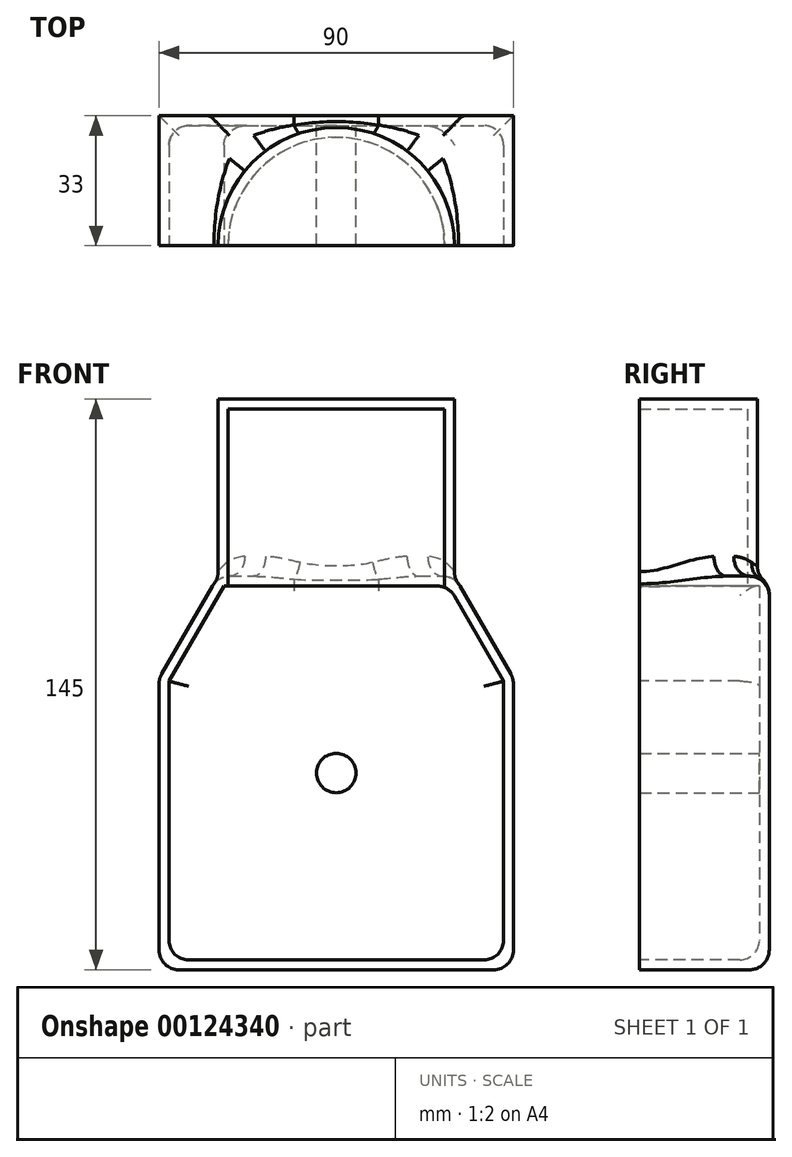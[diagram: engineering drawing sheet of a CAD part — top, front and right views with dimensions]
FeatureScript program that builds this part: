
annotation { "Feature Type Name" : "Feature", "Feature Type Description" : "" }
export const myFeature = defineFeature(function(context is Context, id is Id, definition is map)
    precondition{}
    {
        {
            var Q0;
            Q0=qCreatedBy(makeId("Front.planeOp"),FACE);
            var sketch = newSketch(context, id + "F0", { "sketchPlane" : qUnion([Q0])});
            skLineSegment(sketch, "E0.bottom", {"start": v(-30, 100) * mm, "end": v(30, 100) * mm});
            skLineSegment(sketch, "E0.top", {"start": v(-45, 0) * mm, "end": v(45, 0) * mm});
            skLineSegment(sketch, "E0.left", {"start": v(-45, 74.02) * mm, "end": v(-45, 0) * mm});
            skLineSegment(sketch, "E0.right", {"start": v(45, 74.02) * mm, "end": v(45, 0) * mm});
            skLineSegment(sketch, "E1.top", {"start": v(-30, 145) * mm, "end": v(30, 145) * mm});
            skLineSegment(sketch, "E1.left", {"start": v(-30, 100) * mm, "end": v(-30, 145) * mm});
            skLineSegment(sketch, "E1.right", {"start": v(30, 100) * mm, "end": v(30, 145) * mm});
            skLineSegment(sketch, "E2", {"start": v(0, 0) * mm, "end": v(0, 230.65) * mm, "construction": true});
            skLineSegment(sketch, "E3", {"start": v(-30, 100) * mm, "end": v(-45, 74.02) * mm});
            skLineSegment(sketch, "E4", {"start": v(30, 100) * mm, "end": v(45, 74.02) * mm});
            skLineSegment(sketch, "E5", {"start": v(0, 100) * mm, "end": v(0, 145) * mm});
            skSolve(sketch);
        }
        {
            var Q0;
            {var subQ0=sQuery(id+"F0.wireOp",EDGE,"E1.right");Q0=makeQuery(id+"F0.imprint","IMPRINT",FACE,{"disambiguationData":[TD([[makeQuery(id+"F0.imprint","IMPRINT",EDGE,{"derivedFrom":subQ0}),1.0]])]});}
            var Q1;
            Q1=sQuery(id+"F0.wireOp",EDGE,"E2");
            revolve(context, id + "F1", {"entities" : qUnion([Q0]), "axis" : qUnion([Q1]), "revolveType" : RevolveType.ONE_DIRECTION, "angle" : 180 * degree});
        }
        {
            var Q0;
            Q0=makeQuery(id+"F0.imprint","IMPRINT",FACE,{"disambiguationData":[TD([[makeQuery(id+"F0.imprint","IMPRINT",EDGE,{"derivedFrom":sQuery(id+"F0.wireOp",EDGE,"E0.top")}),1.0]])]});
            extrude(context, id + "F2", {"entities" : qUnion([Q0]), "operationType" : NewBodyOperationType.ADD, "oppositeDirection" : true, "depth" : 33 * mm});
        }
        {
            var Q0;
            {var subQ0=sQuery(id+"F0.wireOp",EDGE,"E0.bottom");Q0=makeQuery(id+"F2.boolean.opBoolean","MERGE",FACE,{"derivedFrom":[makeQuery(id+"F1.opRevolve","CAP_FACE",FACE,{"disambiguationData":[OSD([subQ0,sQuery(id+"F0.wireOp",EDGE,"E1.top"),sQuery(id+"F0.wireOp",EDGE,"E1.right"),sQuery(id+"F0.wireOp",EDGE,"E5")])],"isStart":false}),makeQuery(id+"F2.opExtrude","CAP_FACE",FACE,{"disambiguationData":[OSD([sQuery(id+"F0.wireOp",EDGE,"E0.top"),sQuery(id+"F0.wireOp",EDGE,"E0.left"),sQuery(id+"F0.wireOp",EDGE,"E0.right"),subQ0,sQuery(id+"F0.wireOp",EDGE,"E3"),sQuery(id+"F0.wireOp",EDGE,"E4")])],"isStart":true})]});}
            shell(context, id + "F3", {"entities" : qUnion([Q0]), "thickness" : 2.5 * mm});
        }
        {
            var Q0;
            Q0=makeQuery(id+"F2.opExtrude","SWEPT_EDGE",EDGE,{"disambiguationData":[OSD([sQuery(id+"F0.wireOp",EDGE,"E0.bottom"),sQuery(id+"F0.wireOp",EDGE,"E1.right"),sQuery(id+"F0.wireOp",EDGE,"E4")])]});
            var Q1;
            Q1=makeQuery(id+"F2.opExtrude","SWEPT_EDGE",EDGE,{"disambiguationData":[OSD([sQuery(id+"F0.wireOp",EDGE,"E0.right"),sQuery(id+"F0.wireOp",EDGE,"E4")])]});
            var Q2;
            Q2=makeQuery(id+"F2.opExtrude","SWEPT_EDGE",EDGE,{"disambiguationData":[OSD([sQuery(id+"F0.wireOp",EDGE,"E0.top"),sQuery(id+"F0.wireOp",EDGE,"E0.right")])]});
            var Q3;
            Q3=makeQuery(id+"F2.opExtrude","CAP_EDGE",EDGE,{"disambiguationData":[OSD([sQuery(id+"F0.wireOp",EDGE,"E0.bottom")])],"isStart":false});
            var Q4;
            Q4=makeQuery(id+"F2.opExtrude","CAP_EDGE",EDGE,{"disambiguationData":[OSD([sQuery(id+"F0.wireOp",EDGE,"E0.top")])],"isStart":false});
            var Q5;
            Q5=makeQuery(id+"F2.opExtrude","SWEPT_EDGE",EDGE,{"disambiguationData":[OSD([sQuery(id+"F0.wireOp",EDGE,"E0.bottom"),sQuery(id+"F0.wireOp",EDGE,"E1.left"),sQuery(id+"F0.wireOp",EDGE,"E3")])]});
            var Q6;
            Q6=makeQuery(id+"F2.opExtrude","SWEPT_EDGE",EDGE,{"disambiguationData":[OSD([sQuery(id+"F0.wireOp",EDGE,"E0.left"),sQuery(id+"F0.wireOp",EDGE,"E3")])]});
            var Q7;
            Q7=makeQuery(id+"F2.opExtrude","SWEPT_EDGE",EDGE,{"disambiguationData":[OSD([sQuery(id+"F0.wireOp",EDGE,"E0.top"),sQuery(id+"F0.wireOp",EDGE,"E0.left")])]});
            var Q8;
            {var subQ0=sQuery(id+"F0.wireOp",EDGE,"E0.left");Q8=makeQuery(id+"F3.opShell","OFFSET_EDGE",EDGE,{"disambiguationData":[OSD([subQ0]),TDD([makeQuery(id+"F2.opExtrude","CAP_EDGE",EDGE,{"disambiguationData":[OSD([subQ0])],"isStart":false})])]});}
            var Q9;
            {var subQ0=sQuery(id+"F0.wireOp",EDGE,"E3");Q9=makeQuery(id+"F3.opShell","OFFSET_EDGE",EDGE,{"disambiguationData":[OSD([subQ0]),TDD([makeQuery(id+"F2.opExtrude","CAP_EDGE",EDGE,{"disambiguationData":[OSD([subQ0])],"isStart":false})])]});}
            var Q10;
            {var subQ0=sQuery(id+"F0.wireOp",EDGE,"E4");Q10=makeQuery(id+"F3.opShell","OFFSET_EDGE",EDGE,{"disambiguationData":[OSD([subQ0]),TDD([makeQuery(id+"F2.opExtrude","CAP_EDGE",EDGE,{"disambiguationData":[OSD([subQ0])],"isStart":false})])]});}
            var Q11;
            {var subQ0=sQuery(id+"F0.wireOp",EDGE,"E4");var subQ1=sQuery(id+"F0.wireOp",EDGE,"E1.right");var subQ2=sQuery(id+"F0.wireOp",EDGE,"E0.bottom");Q11=makeQuery(id+"F3.opShell","OFFSET_EDGE",EDGE,{"disambiguationData":[OSD([subQ2,subQ1,subQ0]),TDD([makeQuery(id+"F1.opRevolve","SWEPT_EDGE",EDGE,{"disambiguationData":[OSD([subQ2,subQ1,subQ0])]})])]});}
            var Q12;
            {var subQ0=sQuery(id+"F0.wireOp",EDGE,"E0.right");Q12=makeQuery(id+"F3.opShell","OFFSET_EDGE",EDGE,{"disambiguationData":[OSD([subQ0]),TDD([makeQuery(id+"F2.opExtrude","CAP_EDGE",EDGE,{"disambiguationData":[OSD([subQ0])],"isStart":false})])]});}
            var Q13;
            {var subQ0=sQuery(id+"F0.wireOp",EDGE,"E0.top");Q13=makeQuery(id+"F3.opShell","OFFSET_EDGE",EDGE,{"disambiguationData":[OSD([subQ0]),TDD([makeQuery(id+"F2.opExtrude","CAP_EDGE",EDGE,{"disambiguationData":[OSD([subQ0])],"isStart":false})])]});}
            var Q14;
            Q14=makeQuery(id+"F3.opShell","OFFSET_EDGE",EDGE,{"disambiguationData":[OSD([sQuery(id+"F0.wireOp",EDGE,"E0.top"),sQuery(id+"F0.wireOp",EDGE,"E0.left")])]});
            var Q15;
            Q15=makeQuery(id+"F3.opShell","OFFSET_EDGE",EDGE,{"disambiguationData":[OSD([sQuery(id+"F0.wireOp",EDGE,"E0.top"),sQuery(id+"F0.wireOp",EDGE,"E0.right")])]});
            fillet(context, id + "F4", {"entities" : qUnion([Q0, Q1, Q2, Q3, Q4, Q5, Q6, Q7, Q8, Q9, Q10, Q11, Q12, Q13, Q14, Q15]), "radius" : 5 * mm, "tangentPropagation" : true, "allowEdgeOverflow" : false});
        }
        {
            var Q0;
            Q0=makeQuery(id+"F4.opFillet","BLEND_EDGE",EDGE,{"blendedFrom":[makeQuery(id+"F2.opExtrude","CAP_EDGE",EDGE,{"disambiguationData":[OSD([sQuery(id+"F0.wireOp",EDGE,"E0.bottom")])],"isStart":false}),makeQuery(id+"F1.opRevolve","SWEPT_FACE",FACE,{"disambiguationData":[OSD([sQuery(id+"F0.wireOp",EDGE,"E1.right")])]})],"blendedInto":[makeQuery(id+"F1.opRevolve","SWEPT_FACE",FACE,{"disambiguationData":[OSD([sQuery(id+"F0.wireOp",EDGE,"E1.right")])]})]});
            fillet(context, id + "F5", {"entities" : qUnion([Q0]), "radius" : 5 * mm, "tangentPropagation" : true, "allowEdgeOverflow" : false});
        }
        {
            var Q0;
            Q0=makeQuery(id+"F2.opExtrude","CAP_FACE",FACE,{"disambiguationData":[OSD([sQuery(id+"F0.wireOp",EDGE,"E0.top"),sQuery(id+"F0.wireOp",EDGE,"E0.left"),sQuery(id+"F0.wireOp",EDGE,"E0.right"),sQuery(id+"F0.wireOp",EDGE,"E0.bottom"),sQuery(id+"F0.wireOp",EDGE,"E3"),sQuery(id+"F0.wireOp",EDGE,"E4")])],"isStart":false});
            cPlane(context, id + "F6", {"entities" : qUnion([Q0]), "cplaneType" : CPlaneType.OFFSET, "offset" : 0 * mm, "width" : 150 * mm, "height" : 150 * mm});
        }
        {
            var Q0;
            Q0=qCreatedBy(id+"F6.planeOp",FACE);
            var sketch = newSketch(context, id + "F7", { "sketchPlane" : qUnion([Q0])});
            skCircle(sketch, "E6", {"center": v(0, 50) * mm, "radius": 5 * mm});
            skSolve(sketch);
        }
        {
            var Q0;
            Q0 = qSketchRegion(id + "F7", true);
            extrude(context, id + "F8", {"entities" : qUnion([Q0]), "operationType" : NewBodyOperationType.ADD, "oppositeDirection" : true, "depth" : 32.95 * mm});
        }
    });
